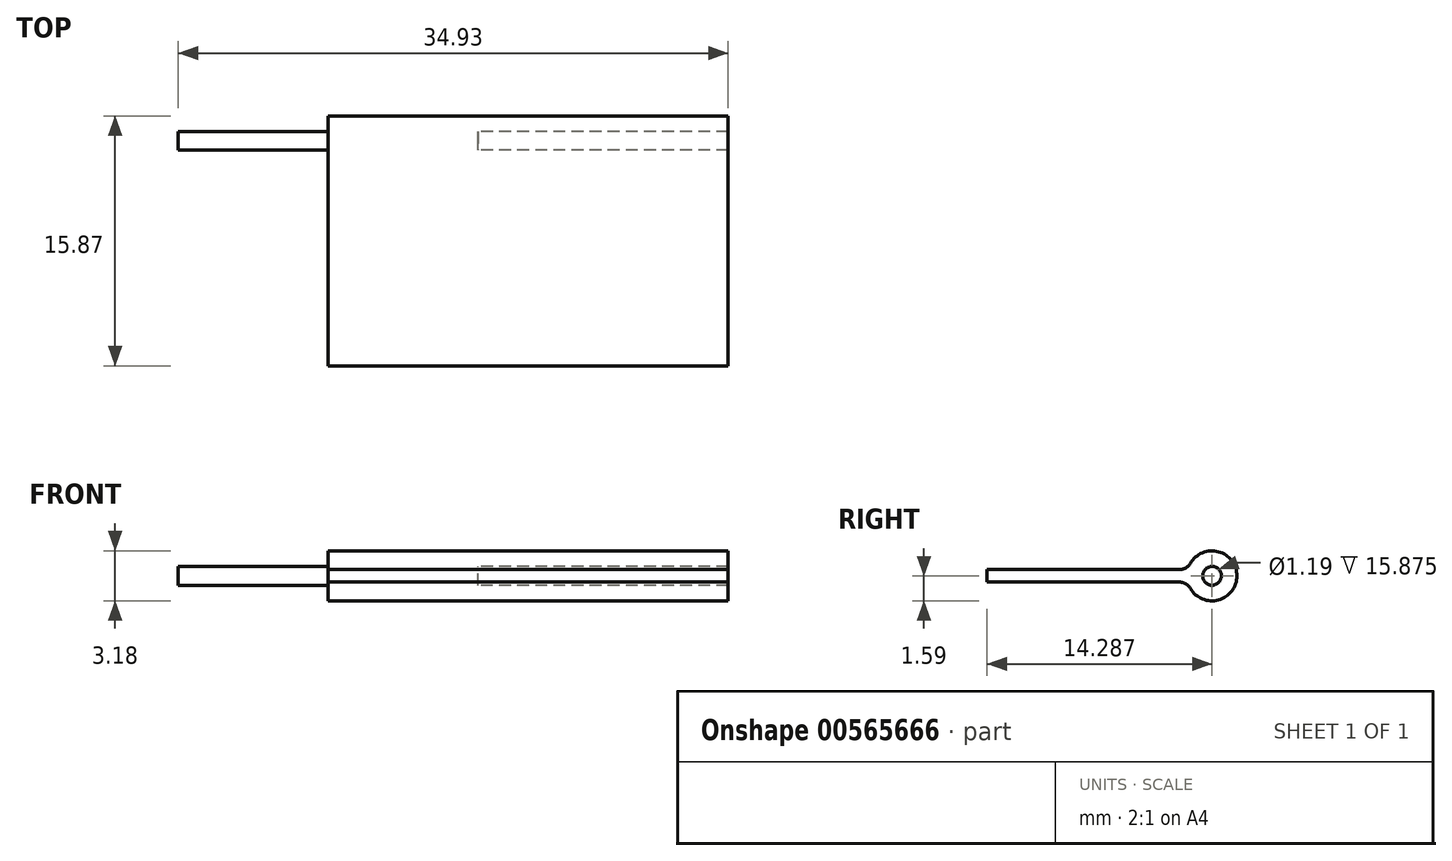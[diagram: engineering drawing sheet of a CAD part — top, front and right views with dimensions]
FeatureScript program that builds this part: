
annotation { "Feature Type Name" : "Feature", "Feature Type Description" : "" }
export const myFeature = defineFeature(function(context is Context, id is Id, definition is map)
    precondition{}
    {
        {
            var Q0;
            Q0=qCreatedBy(makeId("Right.planeOp"),FACE);
            var sketch = newSketch(context, id + "F0", { "sketchPlane" : qUnion([Q0])});
            skLineSegment(sketch, "E0", {"start": v(-12.7, -0.4) * mm, "end": v(-0.47, -0.4) * mm});
            skLineSegment(sketch, "E1", {"start": v(-0.47, 0.4) * mm, "end": v(-12.7, 0.4) * mm});
            skLineSegment(sketch, "E2", {"start": v(-12.7, 0.4) * mm, "end": v(-12.7, -0.4) * mm});
            skCircle(sketch, "E3", {"center": v(1.59, 0) * mm, "radius": 0.6 * mm});
            skArc(sketch, "E4", {"start": v(0.21, -0.8) * mm, "mid": v(3.18, 0) * mm, "end": v(0.21, 0.8) * mm});
            skPoint(sketch, "E5.visualSharp", {"position": v(0.05, 0.4) * mm});
            skArc(sketch, "E5.filletArc", {"start": v(-0.47, 0.4) * mm, "mid": v(-0.08, 0.5) * mm, "end": v(0.21, 0.8) * mm});
            skPoint(sketch, "E6.visualSharp", {"position": v(0.05, -0.4) * mm});
            skArc(sketch, "E6.filletArc", {"start": v(0.21, -0.8) * mm, "mid": v(-0.08, -0.5) * mm, "end": v(-0.47, -0.4) * mm});
            skSolve(sketch);
        }
        {
            var Q0;
            Q0=makeQuery(id+"F0.imprint","IMPRINT",FACE,{"disambiguationData":[TD([[makeQuery(id+"F0.imprint","IMPRINT",EDGE,{"derivedFrom":sQuery(id+"F0.wireOp",EDGE,"E3")}),1.0]])]});
            extrude(context, id + "F1", {"entities" : qUnion([Q0]), "endBound" : BoundingType.SYMMETRIC, "depth" : 19.05 * mm});
        }
        {
            var Q0;
            Q0=makeQuery(id+"F0.imprint","IMPRINT",FACE,{"disambiguationData":[TD([[makeQuery(id+"F0.imprint","IMPRINT",EDGE,{"derivedFrom":sQuery(id+"F0.wireOp",EDGE,"E0")}),1.0]])]});
            extrude(context, id + "F2", {"entities" : qUnion([Q0]), "operationType" : NewBodyOperationType.ADD, "depth" : 25.4 * mm, "offsetDistance" : 25.4 * mm});
        }
    });
